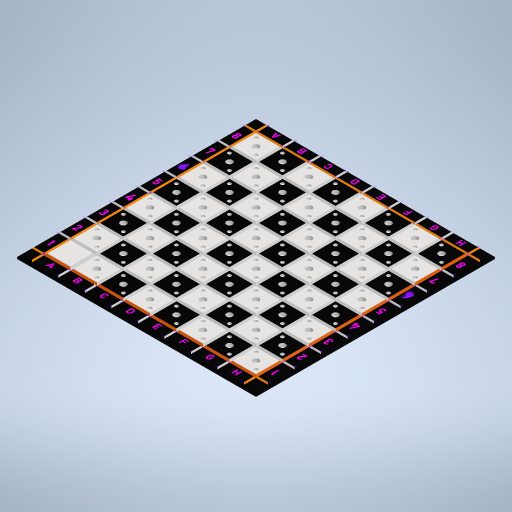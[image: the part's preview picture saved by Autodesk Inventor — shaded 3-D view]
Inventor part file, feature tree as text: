
AUTODESK INVENTOR PART (.ipt)
format: ipt  version: 2024.1 (Build 281209000, 209)  size: 1,915,392 bytes
history: native  units: in
note: dims shown in document units (in); Inventor stores cm internally (conversion verified against a paired STEP export)
features: projected_geometry x14, extrude x11, sketch x11, other x5, chamfer x4, pattern_linear x1
ambient origin geometry x8: Origin, YZ Plane, XZ Plane, XY Plane, X Axis, Y Axis, Z Axis, Center Point
bodies: Body1 (feature_tree), Body2 (feature_tree)
feature tree (46):
  other  "top-plate"
  extrude  "Extrusion1"  Depth=1.0039in
  chamfer  "Chamfer1"  Distance=0.1102in
  extrude  "Extrusion2"  Depth=0.0591in
  pattern_linear  "Rectangular Pattern1"  Count1=8 Spacing1=1.0039in
  extrude  "Extrusion5"  Depth=0.5118in
  extrude  "Extrusion6"  Depth=0.0433in TaperAngle=45.0deg
  extrude  "Extrusion4"  Depth=0.0236in TaperAngle=0.0deg
  chamfer  "Chamfer3"  Distance=0.0394in
  chamfer  "Chamfer4"  [1 undecoded]
  extrude  "Extrusion8"  Depth=0.0118in TaperAngle=0.0deg
  extrude  "Extrusion9"  Depth=0.0472in
  extrude  "Extrusion10"  Depth=0.0472in
  extrude  "Extrusion11"  Depth=0.0472in
  extrude  "Extrusion12"  Depth=0.0472in
  chamfer  "Chamfer5"  Distance=0.1575in
  extrude  "Extrusion13"  Depth=0.0472in
  other  "Work Point1"
  other  "Work Point2"
  other  "Work Point3"
  sketch  "Sketch1"  dims[d0=1.0039in d1=1.0039in d2=0.1102in d3=0.0in]
  sketch  "Sketch2"  dims[d4=0.0591in d5=0.0787in d6=45.0deg d7=0.2362in]
  sketch  "Sketch4"  dims[d8=1.0039in]
  projected_geometry  "Projected Loop1"
  sketch  "Sketch5"  dims[d9=0.502in]
  projected_geometry  "Projected Loop2"
  projected_geometry  "Projected Loop3"
  sketch  "Sketch6"  dims[d10=1.0039in]
  projected_geometry  "Projected Loop4"
  sketch  "Sketch8"  dims[d11=0.502in]
  sketch  "Sketch9"  dims[d12=0.0984in d13=0.0in d23=3.1496in d25=1.0039in]
  projected_geometry  "Projected Loop5"
  projected_geometry  "Projected Loop6"
  projected_geometry  "Projected Loop7"
  projected_geometry  "Projected Loop8"
  projected_geometry  "Projected Loop9"
  projected_geometry  "Projected Loop10"
  projected_geometry  "Projected Loop11"
  projected_geometry  "Projected Loop12"
  projected_geometry  "Projected Loop13"
  sketch  "Sketch10"  dims[d26=3.1496in d28=1.0039in d29=0.5118in]
  sketch  "Sketch11"  dims[d30=0.1575in d31=0.0in d32=0.0433in d33=0.0787in d34=45.0deg]
  sketch  "Sketch12"  dims[d35=0.0984in d36=0.0787in d37=45.0deg d38=0.0236in d39=0.0in d40=0.0394in d41=0.0in d53=0.0in d54=0.0in]
  projected_geometry  "Projected Loop14"
  other  "top-caps"
  sketch  "Sketch13"  dims[d55=0.0in d56=0.0in d57=0.0118in d58=0.0in d59=0.1378in d60=0.1575in d61=0.1575in d62=0.1575in d63=0.1575in d64=3.1496in d66=1.0039in d67=3.1496in d69=1.0039in d72=0.1575in d73=0.1575in d74=0.0591in d75=0.0in d76=0.0157in d77=0.0in d78=0.0157in d79=0.0787in d80=45.0deg d81=0.0079in d82=0.0079in d83=0.0472in d84=0.0in]
note: 1 required parameter value undecoded (feature->parameter linkage not recoverable at this tier; creation-order binding heuristic only, values carry confidence <= 0.55)
